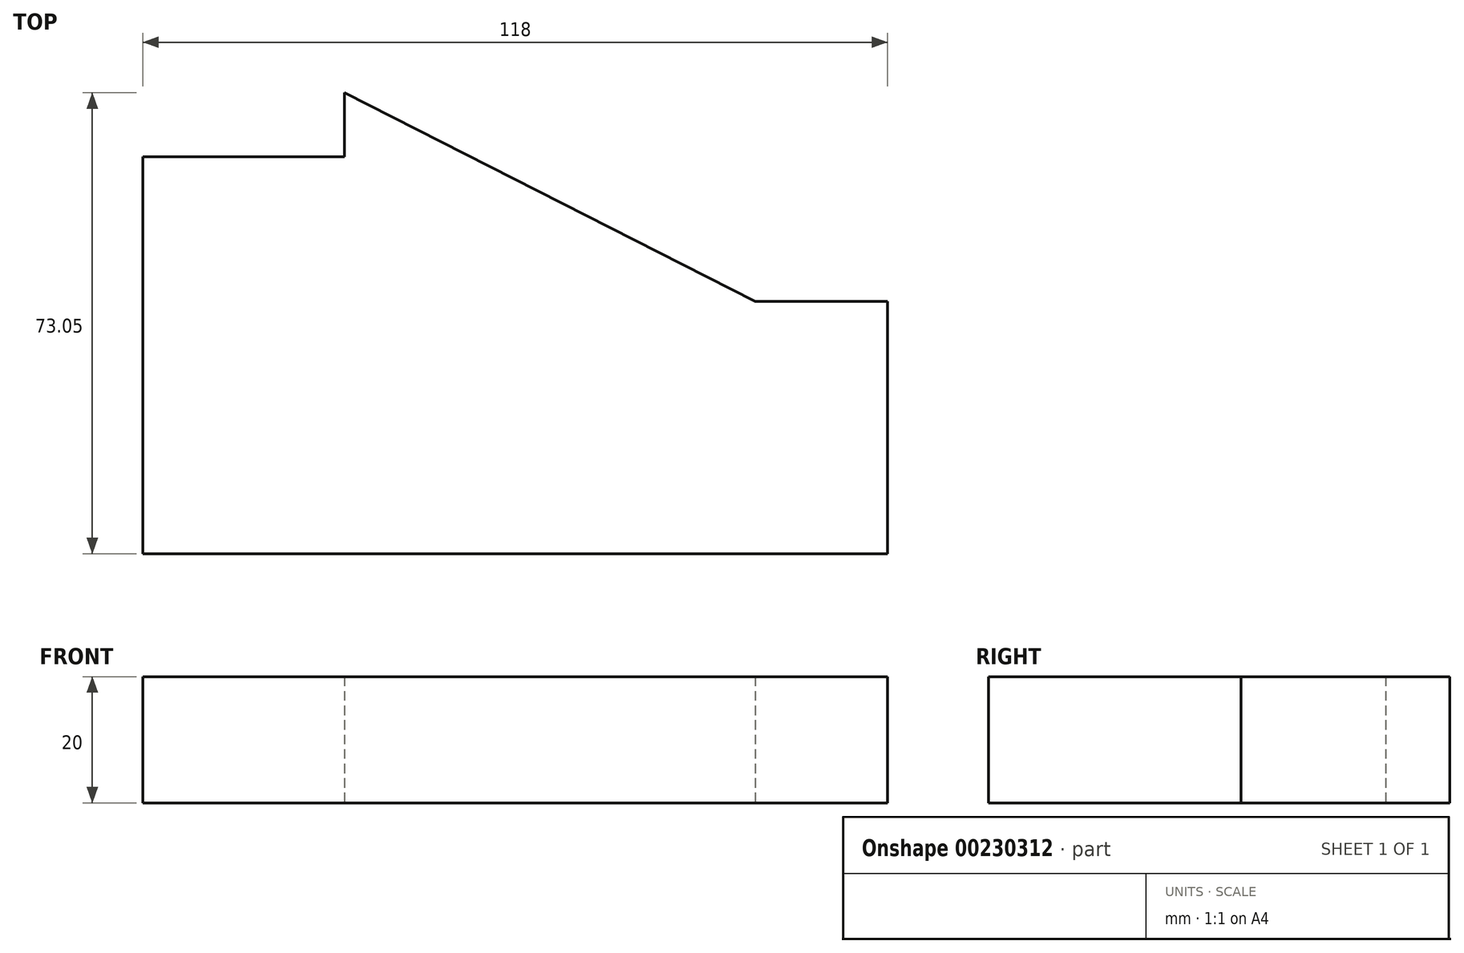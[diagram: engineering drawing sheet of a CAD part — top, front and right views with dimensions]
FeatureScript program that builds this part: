
annotation { "Feature Type Name" : "Feature", "Feature Type Description" : "" }
export const myFeature = defineFeature(function(context is Context, id is Id, definition is map)
    precondition{}
    {
        {
            var Q0;
            Q0=qCreatedBy(makeId("Top.planeOp"),FACE);
            var sketch = newSketch(context, id + "F0", { "sketchPlane" : qUnion([Q0])});
            skLineSegment(sketch, "E0", {"start": v(-3.74, 56.74) * mm, "end": v(61.34, 23.69) * mm});
            skLineSegment(sketch, "E1", {"start": v(61.34, 23.69) * mm, "end": v(82.34, 23.69) * mm});
            skLineSegment(sketch, "E2", {"start": v(82.34, 23.69) * mm, "end": v(82.34, -16.31) * mm});
            skLineSegment(sketch, "E3", {"start": v(82.34, -16.31) * mm, "end": v(-35.66, -16.31) * mm});
            skLineSegment(sketch, "E4", {"start": v(-35.66, -16.31) * mm, "end": v(-35.66, 46.58) * mm});
            skLineSegment(sketch, "E5", {"start": v(-35.66, 46.58) * mm, "end": v(-3.74, 46.58) * mm});
            skLineSegment(sketch, "E6", {"start": v(-3.74, 46.58) * mm, "end": v(-3.74, 56.74) * mm});
            skSolve(sketch);
        }
        {
            var Q0;
            Q0=makeQuery(id+"F0.imprint","IMPRINT",FACE,{"disambiguationData":[TD([[makeQuery(id+"F0.imprint","IMPRINT",EDGE,{"derivedFrom":sQuery(id+"F0.wireOp",EDGE,"E0")}),-1.0]])]});
            extrude(context, id + "F1", {"entities" : qUnion([Q0]), "depth" : 20 * mm});
        }
    });
